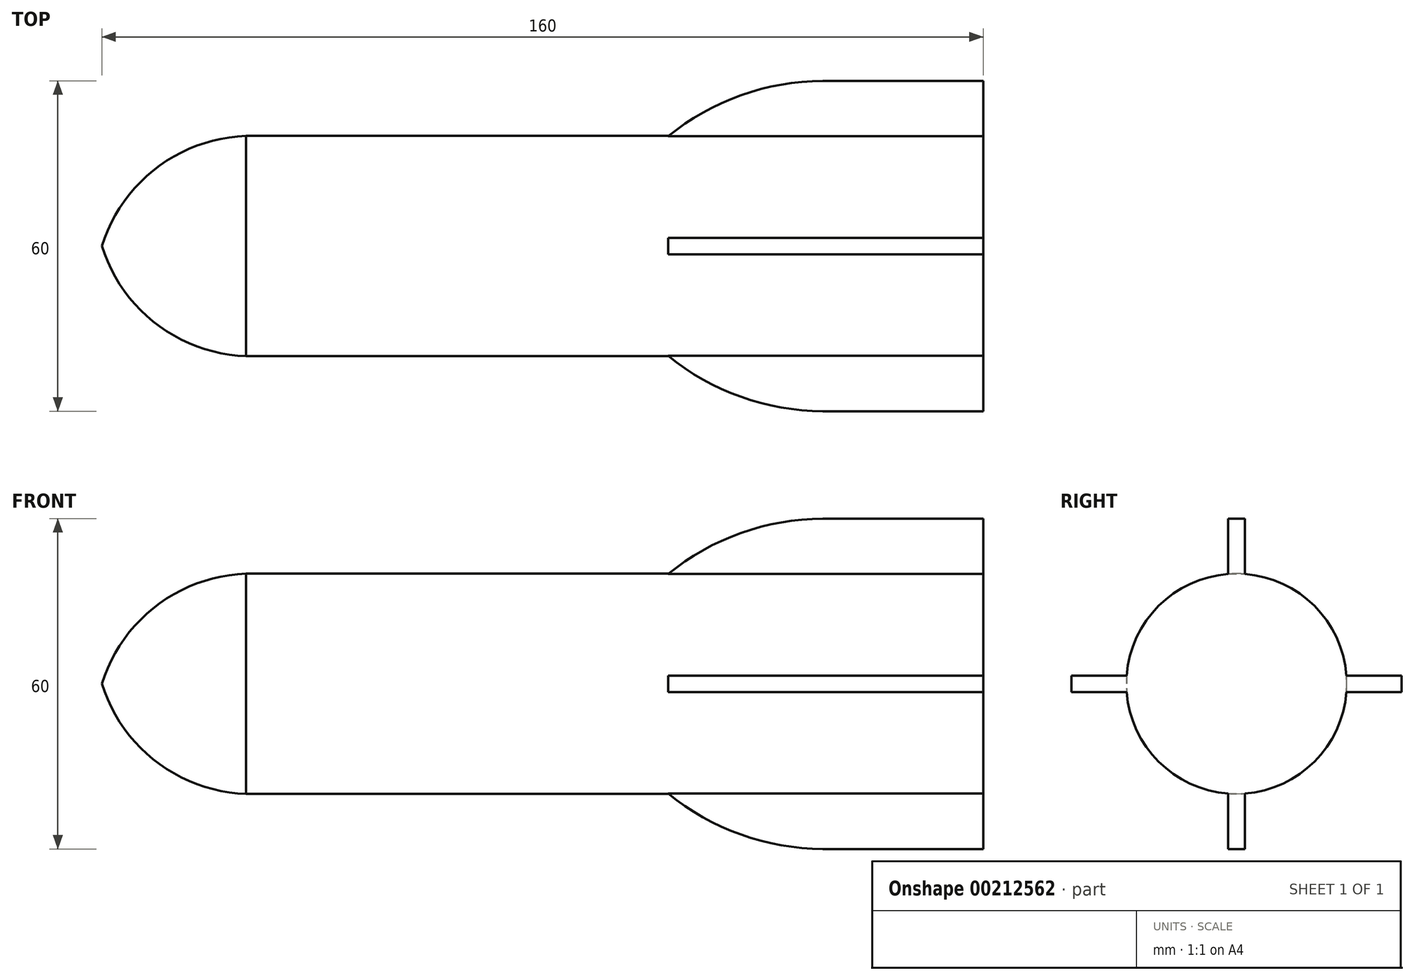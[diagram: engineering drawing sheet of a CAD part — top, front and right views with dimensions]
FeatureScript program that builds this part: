
annotation { "Feature Type Name" : "Feature", "Feature Type Description" : "" }
export const myFeature = defineFeature(function(context is Context, id is Id, definition is map)
    precondition{}
    {
        {
            var Q0;
            Q0=qCreatedBy(makeId("Front.planeOp"),FACE);
            var sketch = newSketch(context, id + "F0", { "sketchPlane" : qUnion([Q0])});
            skLineSegment(sketch, "E0.bottom", {"start": v(0, 0) * mm, "end": v(160, 0) * mm});
            skLineSegment(sketch, "E0.top", {"start": v(0, 20) * mm, "end": v(160, 20) * mm});
            skLineSegment(sketch, "E0.left", {"start": v(0, 0) * mm, "end": v(0, 20) * mm});
            skLineSegment(sketch, "E0.right", {"start": v(160, 0) * mm, "end": v(160, 20) * mm});
            skArc(sketch, "E1", {"start": v(28.21, 20) * mm, "mid": v(10.72, 14.78) * mm, "end": v(0, 0) * mm});
            skSolve(sketch);
        }
        {
            var Q0;
            {var subQ5=sQuery(id+"F0.wireOp",EDGE,"E0.bottom");Q0=makeQuery(id+"F0.imprint","IMPRINT",FACE,{"disambiguationData":[TD([[makeQuery(id+"F0.imprint","IMPRINT",EDGE,{"derivedFrom":subQ5}),1.0]])]});}
            var Q1;
            Q1=sQuery(id+"F0.wireOp",EDGE,"E0.bottom");
            revolve(context, id + "F1", {"entities" : qUnion([Q0]), "axis" : qUnion([Q1]), "revolveType" : RevolveType.FULL});
        }
        {
            var Q0;
            Q0=makeQuery(id+"F1.opRevolve","SWEPT_FACE",FACE,{"disambiguationData":[OSD([sQuery(id+"F0.wireOp",EDGE,"E0.right")])]});
            var sketch = newSketch(context, id + "F2", { "sketchPlane" : qUnion([Q0])});
            skPoint(sketch, "E2", {"position": v(-20, 0) * mm});
            skLineSegment(sketch, "E3.bottom", {"start": v(-30, 1.5) * mm, "end": v(-10, 1.5) * mm});
            skLineSegment(sketch, "E3.top", {"start": v(-30, -1.5) * mm, "end": v(-10, -1.5) * mm});
            skLineSegment(sketch, "E3.left", {"start": v(-30, 1.5) * mm, "end": v(-30, -1.5) * mm});
            skLineSegment(sketch, "E3.right", {"start": v(-10, 1.5) * mm, "end": v(-10, -1.5) * mm});
            skPoint(sketch, "E4", {"position": v(0, 20) * mm});
            skPoint(sketch, "E5", {"position": v(20, 0) * mm});
            skPoint(sketch, "E6", {"position": v(0, -20) * mm});
            skLineSegment(sketch, "E7.bottom", {"start": v(1.5, 10) * mm, "end": v(-1.5, 10) * mm});
            skLineSegment(sketch, "E7.top", {"start": v(1.5, 30) * mm, "end": v(-1.5, 30) * mm});
            skLineSegment(sketch, "E7.left", {"start": v(1.5, 10) * mm, "end": v(1.5, 30) * mm});
            skLineSegment(sketch, "E7.right", {"start": v(-1.5, 10) * mm, "end": v(-1.5, 30) * mm});
            skLineSegment(sketch, "E8.bottom", {"start": v(30, -1.5) * mm, "end": v(10, -1.5) * mm});
            skLineSegment(sketch, "E8.top", {"start": v(30, 1.5) * mm, "end": v(10, 1.5) * mm});
            skLineSegment(sketch, "E8.left", {"start": v(30, -1.5) * mm, "end": v(30, 1.5) * mm});
            skLineSegment(sketch, "E8.right", {"start": v(10, -1.5) * mm, "end": v(10, 1.5) * mm});
            skLineSegment(sketch, "E9.bottom", {"start": v(1.5, -30) * mm, "end": v(-1.5, -30) * mm});
            skLineSegment(sketch, "E9.top", {"start": v(1.5, -10) * mm, "end": v(-1.5, -10) * mm});
            skLineSegment(sketch, "E9.left", {"start": v(1.5, -30) * mm, "end": v(1.5, -10) * mm});
            skLineSegment(sketch, "E9.right", {"start": v(-1.5, -30) * mm, "end": v(-1.5, -10) * mm});
            skSolve(sketch);
        }
        {
            var Q0;
            {var subQ0=sQuery(id+"F2.wireOp",EDGE,"E7.top");Q0=makeQuery(id+"F2.imprint","IMPRINT",FACE,{"disambiguationData":[TD([[makeQuery(id+"F2.imprint","IMPRINT",EDGE,{"derivedFrom":subQ0}),1.0]])]});}
            var Q1;
            {var subQ0=sQuery(id+"F2.wireOp",EDGE,"E8.left");Q1=makeQuery(id+"F2.imprint","IMPRINT",FACE,{"disambiguationData":[TD([[makeQuery(id+"F2.imprint","IMPRINT",EDGE,{"derivedFrom":subQ0}),1.0]])]});}
            var Q2;
            {var subQ0=sQuery(id+"F2.wireOp",EDGE,"E9.bottom");Q2=makeQuery(id+"F2.imprint","IMPRINT",FACE,{"disambiguationData":[TD([[makeQuery(id+"F2.imprint","IMPRINT",EDGE,{"derivedFrom":subQ0}),-1.0]])]});}
            var Q3;
            {var subQ0=sQuery(id+"F2.wireOp",EDGE,"E3.left");Q3=makeQuery(id+"F2.imprint","IMPRINT",FACE,{"disambiguationData":[TD([[makeQuery(id+"F2.imprint","IMPRINT",EDGE,{"derivedFrom":subQ0}),1.0]])]});}
            extrude(context, id + "F3", {"entities" : qUnion([Q0, Q1, Q2, Q3]), "operationType" : NewBodyOperationType.ADD, "oppositeDirection" : true, "depth" : 57.2 * mm});
        }
        {
            var Q0;
            Q0=makeQuery(id+"F3.opExtrude","SWEPT_FACE",FACE,{"disambiguationData":[OSD([sQuery(id+"F2.wireOp",EDGE,"E7.left")])]});
            var sketch = newSketch(context, id + "F4", { "sketchPlane" : qUnion([Q0])});
            skLineSegment(sketch, "E10", {"start": v(-102.8, 30) * mm, "end": v(-131.4, 30) * mm});
            skPoint(sketch, "E11", {"position": v(-131.4, 30) * mm});
            skPoint(sketch, "E12", {"position": v(-102.8, 19.94) * mm});
            skPoint(sketch, "E13", {"position": v(-102.8, -20.3) * mm});
            skArc(sketch, "E14", {"start": v(-102.8, 19.94) * mm, "mid": v(-116.23, 27.45) * mm, "end": v(-131.4, 30) * mm});
            skSolve(sketch);
        }
        {
            var Q0;
            {var subQ1=sQuery(id+"F2.wireOp",EDGE,"E7.left");var subQ2=makeQuery(id+"F3.opExtrude","CAP_EDGE",EDGE,{"disambiguationData":[OSD([subQ1])],"isStart":false});Q0=makeQuery(id+"F4.imprint","IMPRINT",FACE,{"disambiguationData":[TD([[makeQuery(id+"F4.imprint","IMPRINT",EDGE,{"derivedFrom":subQ2}),1.0]])]});}
            extrude(context, id + "F5", {"entities" : qUnion([Q0]), "operationType" : NewBodyOperationType.REMOVE, "endBound" : BoundingType.THROUGH_ALL, "oppositeDirection" : true, "depth" : 25 * mm});
        }
        {
            var Q0;
            Q0=makeQuery(id+"F3.opExtrude","SWEPT_FACE",FACE,{"disambiguationData":[OSD([sQuery(id+"F2.wireOp",EDGE,"E9.left")])]});
            var sketch = newSketch(context, id + "F6", { "sketchPlane" : qUnion([Q0])});
            skLineSegment(sketch, "E15", {"start": v(-102.8, -30) * mm, "end": v(-131.4, -30) * mm});
            skPoint(sketch, "E16", {"position": v(-131.4, -30) * mm});
            skPoint(sketch, "E17", {"position": v(-102.8, -30) * mm});
            skPoint(sketch, "E18", {"position": v(-102.8, -19.94) * mm});
            skArc(sketch, "E19", {"start": v(-131.4, -30) * mm, "mid": v(-116.23, -27.45) * mm, "end": v(-102.8, -19.94) * mm});
            skSolve(sketch);
        }
        {
            var Q0;
            {var subQ1=sQuery(id+"F2.wireOp",EDGE,"E9.left");var subQ2=makeQuery(id+"F3.opExtrude","CAP_EDGE",EDGE,{"disambiguationData":[OSD([subQ1])],"isStart":false});Q0=makeQuery(id+"F6.imprint","IMPRINT",FACE,{"disambiguationData":[TD([[makeQuery(id+"F6.imprint","IMPRINT",EDGE,{"derivedFrom":subQ2}),1.0]])]});}
            extrude(context, id + "F7", {"entities" : qUnion([Q0]), "operationType" : NewBodyOperationType.REMOVE, "oppositeDirection" : true, "depth" : 25 * mm});
        }
        {
            var Q0;
            Q0=makeQuery(id+"F3.opExtrude","SWEPT_FACE",FACE,{"disambiguationData":[OSD([sQuery(id+"F2.wireOp",EDGE,"E8.bottom")])]});
            var sketch = newSketch(context, id + "F8", { "sketchPlane" : qUnion([Q0])});
            skLineSegment(sketch, "E20", {"start": v(102.8, -30) * mm, "end": v(131.4, -30) * mm});
            skPoint(sketch, "E21", {"position": v(131.4, -30) * mm});
            skPoint(sketch, "E22", {"position": v(102.8, -30) * mm});
            skPoint(sketch, "E23", {"position": v(102.8, -19.94) * mm});
            skArc(sketch, "E24", {"start": v(102.8, -19.94) * mm, "mid": v(116.23, -27.45) * mm, "end": v(131.4, -30) * mm});
            skSolve(sketch);
        }
        {
            var Q0;
            {var subQ1=sQuery(id+"F2.wireOp",EDGE,"E8.bottom");var subQ2=makeQuery(id+"F3.opExtrude","CAP_EDGE",EDGE,{"disambiguationData":[OSD([subQ1])],"isStart":false});Q0=makeQuery(id+"F8.imprint","IMPRINT",FACE,{"disambiguationData":[TD([[makeQuery(id+"F8.imprint","IMPRINT",EDGE,{"derivedFrom":subQ2}),-1.0]])]});}
            extrude(context, id + "F9", {"entities" : qUnion([Q0]), "operationType" : NewBodyOperationType.REMOVE, "oppositeDirection" : true, "depth" : 25 * mm});
        }
        {
            var Q0;
            Q0=makeQuery(id+"F3.opExtrude","SWEPT_FACE",FACE,{"disambiguationData":[OSD([sQuery(id+"F2.wireOp",EDGE,"E3.top")])]});
            var sketch = newSketch(context, id + "F10", { "sketchPlane" : qUnion([Q0])});
            skLineSegment(sketch, "E25", {"start": v(102.8, 30) * mm, "end": v(131.4, 30) * mm});
            skPoint(sketch, "E26", {"position": v(131.4, 30) * mm});
            skPoint(sketch, "E27", {"position": v(102.8, 30) * mm});
            skPoint(sketch, "E28", {"position": v(102.8, 19.94) * mm});
            skArc(sketch, "E29", {"start": v(131.4, 30) * mm, "mid": v(116.23, 27.45) * mm, "end": v(102.8, 19.94) * mm});
            skSolve(sketch);
        }
        {
            var Q0;
            {var subQ1=sQuery(id+"F2.wireOp",EDGE,"E3.top");var subQ2=makeQuery(id+"F3.opExtrude","CAP_EDGE",EDGE,{"disambiguationData":[OSD([subQ1])],"isStart":false});Q0=makeQuery(id+"F10.imprint","IMPRINT",FACE,{"disambiguationData":[TD([[makeQuery(id+"F10.imprint","IMPRINT",EDGE,{"derivedFrom":subQ2}),1.0]])]});}
            extrude(context, id + "F11", {"entities" : qUnion([Q0]), "operationType" : NewBodyOperationType.REMOVE, "oppositeDirection" : true, "depth" : 25 * mm});
        }
    });
